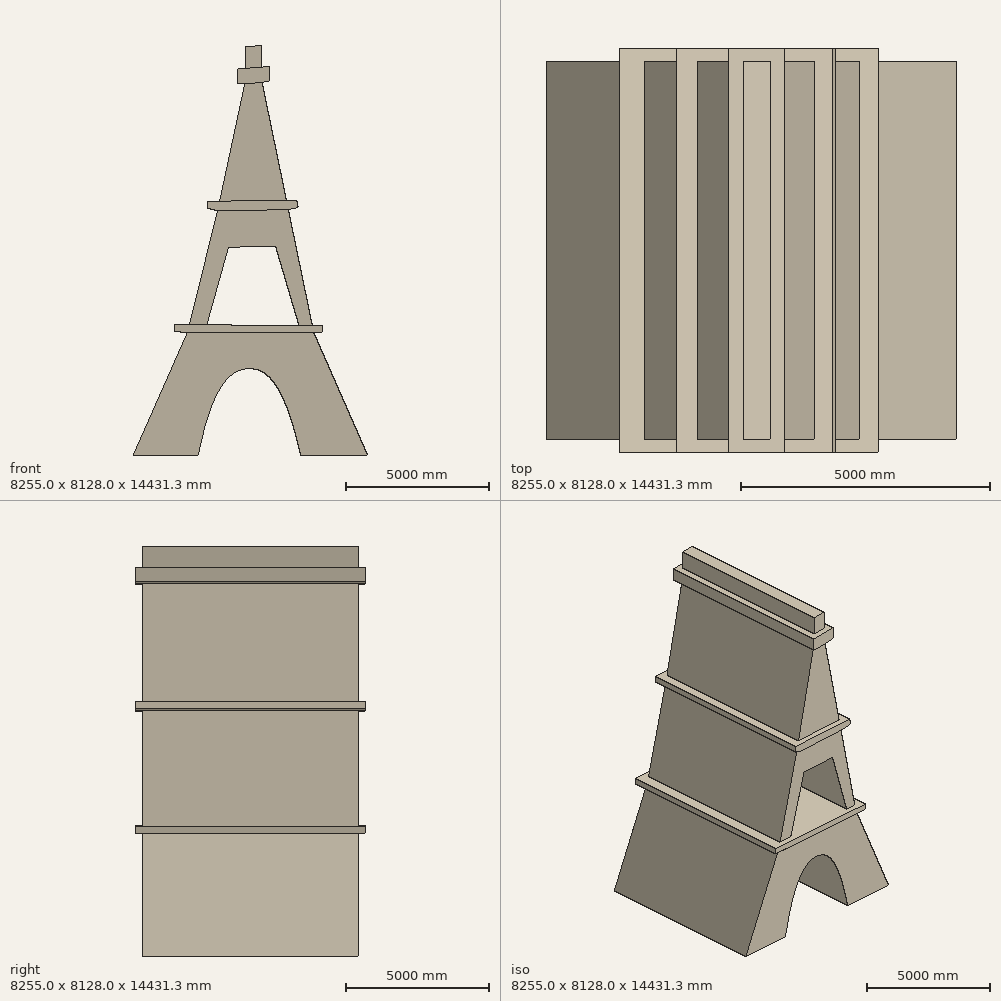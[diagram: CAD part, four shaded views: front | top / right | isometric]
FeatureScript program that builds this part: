
annotation { "Feature Type Name" : "Feature", "Feature Type Description" : "" }
export const myFeature = defineFeature(function(context is Context, id is Id, definition is map)
    precondition{}
    {
        {
            var Q0;
            Q0=qCreatedBy(makeId("Front.planeOp"),FACE);
            var sketch = newSketch(context, id + "F0", { "sketchPlane" : qUnion([Q0])});
            skLineSegment(sketch, "E0", {"start": v(-76.2, 0) * mm, "end": v(2286, 0) * mm});
            skLineSegment(sketch, "E1", {"start": v(5892.8, 0) * mm, "end": v(8255, 0) * mm});
            skFitSpline(sketch, "E2", {"points": [v(2286, 0) * mm, v(4107.27, 3056.9) * mm, v(5892.8, 0) * mm], "startDerivative": vector(2836.35, 14723.92) * mm, "endDerivative": vector(3256.41, -14667.8) * mm});
            skLineSegment(sketch, "E3", {"start": v(0, 0) * mm, "end": v(1909.84, 4321.17) * mm});
            skLineSegment(sketch, "E4", {"start": v(6354.84, 4325.43) * mm, "end": v(8255, 0) * mm});
            skLineSegment(sketch, "E5", {"start": v(1909.84, 4321.17) * mm, "end": v(6354.84, 4325.43) * mm});
            skLineSegment(sketch, "E6", {"start": v(1469.14, 4347.87) * mm, "end": v(6676.09, 4325.43) * mm});
            skLineSegment(sketch, "E7", {"start": v(1469.14, 4347.87) * mm, "end": v(1469.14, 4601.87) * mm});
            skLineSegment(sketch, "E8", {"start": v(6676.09, 4325.43) * mm, "end": v(6676.09, 4579.43) * mm});
            skLineSegment(sketch, "E9", {"start": v(6676.09, 4579.43) * mm, "end": v(1469.14, 4601.87) * mm});
            skLineSegment(sketch, "E10", {"start": v(1909.84, 4321.17) * mm, "end": v(2971.76, 8611.3) * mm});
            skLineSegment(sketch, "E11", {"start": v(6354.84, 4325.43) * mm, "end": v(5460.6, 8653.62) * mm});
            skLineSegment(sketch, "E12", {"start": v(5460.6, 8653.62) * mm, "end": v(2971.76, 8611.3) * mm});
            skLineSegment(sketch, "E13", {"start": v(3359.32, 7331.62) * mm, "end": v(5010.08, 7359.7) * mm});
            skLineSegment(sketch, "E14", {"start": v(2594.05, 4597.02) * mm, "end": v(3359.32, 7331.62) * mm});
            skLineSegment(sketch, "E15", {"start": v(5010.08, 7359.7) * mm, "end": v(5830.48, 4583.07) * mm});
            skLineSegment(sketch, "E16", {"start": v(2971.76, 8611.3) * mm, "end": v(2621.26, 8698.05) * mm});
            skLineSegment(sketch, "E17", {"start": v(5460.6, 8653.62) * mm, "end": v(5808.85, 8725.57) * mm});
            skLineSegment(sketch, "E18", {"start": v(2621.26, 8698.05) * mm, "end": v(2621.26, 8952.05) * mm});
            skLineSegment(sketch, "E19", {"start": v(5808.85, 8725.57) * mm, "end": v(5757.45, 8974.31) * mm});
            skLineSegment(sketch, "E20", {"start": v(5757.45, 8974.31) * mm, "end": v(2621.26, 8952.05) * mm});
            skLineSegment(sketch, "E21", {"start": v(2971.76, 8611.3) * mm, "end": v(3927.89, 13082.2) * mm});
            skLineSegment(sketch, "E22", {"start": v(5460.6, 8653.62) * mm, "end": v(4535.53, 13131.05) * mm});
            skLineSegment(sketch, "E23", {"start": v(3927.89, 13082.2) * mm, "end": v(4535.53, 13131.05) * mm});
            skLineSegment(sketch, "E24", {"start": v(3674.16, 13093.87) * mm, "end": v(3927.89, 13082.2) * mm});
            skLineSegment(sketch, "E25", {"start": v(4535.53, 13131.05) * mm, "end": v(4784.27, 13182.44) * mm});
            skLineSegment(sketch, "E26", {"start": v(3674.16, 13093.87) * mm, "end": v(3674.16, 13601.87) * mm});
            skLineSegment(sketch, "E27", {"start": v(4784.27, 13182.44) * mm, "end": v(4784.27, 13690.44) * mm});
            skLineSegment(sketch, "E28", {"start": v(4784.27, 13690.44) * mm, "end": v(3674.16, 13601.87) * mm});
            skLineSegment(sketch, "E29", {"start": v(3962.3, 13624.86) * mm, "end": v(3962.3, 14386.86) * mm});
            skLineSegment(sketch, "E30", {"start": v(4519.32, 13669.3) * mm, "end": v(4519.32, 14431.3) * mm});
            skLineSegment(sketch, "E31", {"start": v(4519.32, 14431.3) * mm, "end": v(3962.3, 14386.86) * mm});
            skSolve(sketch);
        }
        {
            var Q0;
            {var subQ0=sQuery(id+"F0.wireOp",EDGE,"E29");Q0=makeQuery(id+"F0.imprint","IMPRINT",FACE,{"disambiguationData":[TD([[makeQuery(id+"F0.imprint","IMPRINT",EDGE,{"derivedFrom":subQ0}),-1.0]])]});}
            var Q1;
            {var subQ5=sQuery(id+"F0.wireOp",EDGE,"E23");Q1=makeQuery(id+"F0.imprint","IMPRINT",FACE,{"disambiguationData":[TD([[makeQuery(id+"F0.imprint","IMPRINT",EDGE,{"derivedFrom":subQ5}),-1.0]])]});}
            var Q2;
            {var subQ0=sQuery(id+"F0.wireOp",EDGE,"E12");Q2=makeQuery(id+"F0.imprint","IMPRINT",FACE,{"disambiguationData":[TD([[makeQuery(id+"F0.imprint","IMPRINT",EDGE,{"derivedFrom":subQ0}),1.0]])]});}
            var Q3;
            Q3=makeQuery(id+"F0.imprint","IMPRINT",FACE,{"disambiguationData":[TD([[makeQuery(id+"F0.imprint","IMPRINT",EDGE,{"derivedFrom":sQuery(id+"F0.wireOp",EDGE,"E1")}),1.0]])]});
            extrude(context, id + "F1", {"entities" : qUnion([Q0, Q1, Q2, Q3]), "endBound" : BoundingType.SYMMETRIC, "depth" : 7620 * mm, "offsetDistance" : 25.4 * mm});
        }
        {
            var Q0;
            {var subQ2=sQuery(id+"F0.wireOp",EDGE,"E10");var subQ7=sQuery(id+"F0.wireOp",EDGE,"E6");var subQ8=makeQuery(id+"F0.imprint","INTERSECT",VERTEX,{"derivedFrom":[subQ7,subQ2]});Q0=makeQuery(id+"F0.imprint","IMPRINT",FACE,{"disambiguationData":[TD([[makeQuery(id+"F0.imprint","IMPRINT",EDGE,{"disambiguationData":[TD([[subQ8,-1.0]])],"derivedFrom":subQ7}),1.0]])]});}
            var Q1;
            {var subQ0=sQuery(id+"F0.wireOp",EDGE,"E7");Q1=makeQuery(id+"F0.imprint","IMPRINT",FACE,{"disambiguationData":[TD([[makeQuery(id+"F0.imprint","IMPRINT",EDGE,{"derivedFrom":subQ0}),-1.0]])]});}
            var Q2;
            {var subQ0=sQuery(id+"F0.wireOp",EDGE,"E8");Q2=makeQuery(id+"F0.imprint","IMPRINT",FACE,{"disambiguationData":[TD([[makeQuery(id+"F0.imprint","IMPRINT",EDGE,{"derivedFrom":subQ0}),1.0]])]});}
            extrude(context, id + "F2", {"entities" : qUnion([Q0, Q1, Q2]), "operationType" : NewBodyOperationType.ADD, "endBound" : BoundingType.SYMMETRIC, "depth" : 8128 * mm, "offsetDistance" : 25.4 * mm});
        }
        {
            var Q0;
            {var subQ0=sQuery(id+"F0.wireOp",EDGE,"E12");Q0=makeQuery(id+"F0.imprint","IMPRINT",FACE,{"disambiguationData":[TD([[makeQuery(id+"F0.imprint","IMPRINT",EDGE,{"derivedFrom":subQ0}),-1.0]])]});}
            var Q1;
            {var subQ0=sQuery(id+"F0.wireOp",EDGE,"E17");Q1=makeQuery(id+"F0.imprint","IMPRINT",FACE,{"disambiguationData":[TD([[makeQuery(id+"F0.imprint","IMPRINT",EDGE,{"derivedFrom":subQ0}),1.0]])]});}
            var Q2;
            {var subQ0=sQuery(id+"F0.wireOp",EDGE,"E16");Q2=makeQuery(id+"F0.imprint","IMPRINT",FACE,{"disambiguationData":[TD([[makeQuery(id+"F0.imprint","IMPRINT",EDGE,{"derivedFrom":subQ0}),-1.0]])]});}
            var Q3;
            Q3=makeQuery(id+"F0.imprint","IMPRINT",FACE,{"disambiguationData":[TD([[makeQuery(id+"F0.imprint","IMPRINT",EDGE,{"derivedFrom":sQuery(id+"F0.wireOp",EDGE,"E23")}),1.0]])]});
            extrude(context, id + "F3", {"entities" : qUnion([Q0, Q1, Q2, Q3]), "endBound" : BoundingType.SYMMETRIC, "depth" : 8128 * mm, "offsetDistance" : 25.4 * mm});
        }
    });
